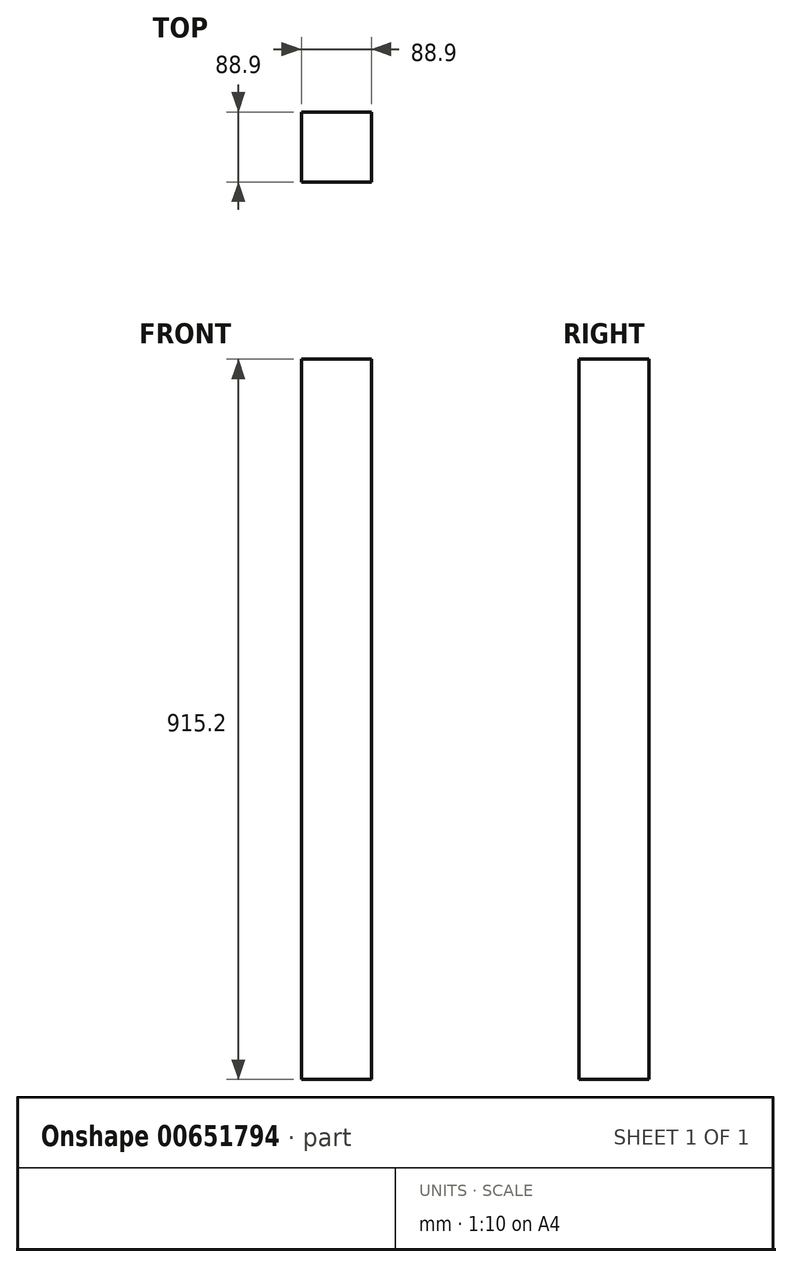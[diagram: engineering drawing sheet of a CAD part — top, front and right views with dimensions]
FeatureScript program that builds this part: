
annotation { "Feature Type Name" : "Feature", "Feature Type Description" : "" }
export const myFeature = defineFeature(function(context is Context, id is Id, definition is map)
    precondition{}
    {
        {
            var Q0;
            Q0=qCreatedBy(makeId("Top.planeOp"),FACE);
            var sketch = newSketch(context, id + "F0", { "sketchPlane" : qUnion([Q0])});
            skLineSegment(sketch, "E0.bottom", {"start": v(0, 0) * mm, "end": v(88.9, 0) * mm});
            skLineSegment(sketch, "E0.top", {"start": v(0, 88.9) * mm, "end": v(88.9, 88.9) * mm});
            skLineSegment(sketch, "E0.left", {"start": v(0, 0) * mm, "end": v(0, 88.9) * mm});
            skLineSegment(sketch, "E0.right", {"start": v(88.9, 0) * mm, "end": v(88.9, 88.9) * mm});
            skSolve(sketch);
        }
        {
            var Q0;
            Q0=makeQuery(id+"F0.imprint","IMPRINT",FACE,{"disambiguationData":[TD([[makeQuery(id+"F0.imprint","IMPRINT",EDGE,{"derivedFrom":sQuery(id+"F0.wireOp",EDGE,"E0.bottom")}),1.0]])]});
            extrude(context, id + "F1", {"entities" : qUnion([Q0]), "depth" : 915.2 * mm, "offsetDistance" : 25.4 * mm});
        }
    });
